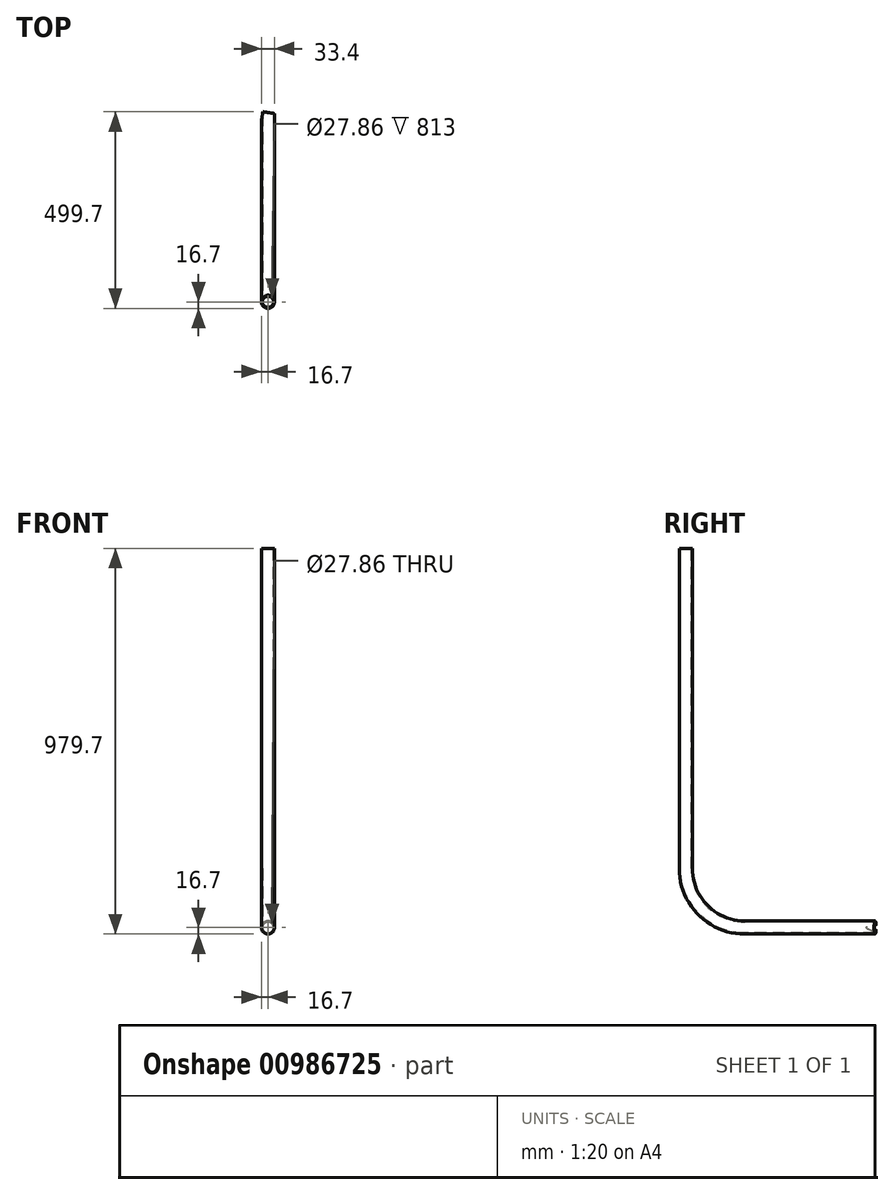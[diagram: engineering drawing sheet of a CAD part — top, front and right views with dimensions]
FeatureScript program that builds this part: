
annotation { "Feature Type Name" : "Feature", "Feature Type Description" : "" }
export const myFeature = defineFeature(function(context is Context, id is Id, definition is map)
    precondition{}
    {
        {
            var Q0;
            Q0=qCreatedBy(makeId("Right.planeOp"),FACE);
            var sketch = newSketch(context, id + "F0", { "sketchPlane" : qUnion([Q0])});
            skLineSegment(sketch, "E0", {"start": v(0, 0) * mm, "end": v(-333.6, 0) * mm});
            skLineSegment(sketch, "E1", {"start": v(-483.6, 150) * mm, "end": v(-483.6, 963) * mm});
            skPoint(sketch, "E2.visualSharp", {"position": v(-483.6, 0) * mm});
            skArc(sketch, "E2.filletArc", {"start": v(-483.6, 150) * mm, "mid": v(-439.67, 43.93) * mm, "end": v(-333.6, 0) * mm});
            skSolve(sketch);
        }
        {
            var Q0;
            Q0=qCreatedBy(makeId("Front.planeOp"),FACE);
            var sketch = newSketch(context, id + "F1", { "sketchPlane" : qUnion([Q0])});
            skCircle(sketch, "E3", {"center": v(0, 0) * mm, "radius": 16.7 * mm});
            skCircle(sketch, "E4.0", {"center": v(0, 0) * mm, "radius": 13.93 * mm});
            skSolve(sketch);
        }
        {
            var Q0;
            Q0=makeQuery(id+"F1.imprint","IMPRINT",FACE,{"disambiguationData":[TD([[makeQuery(id+"F1.imprint","IMPRINT",EDGE,{"derivedFrom":sQuery(id+"F1.wireOp",EDGE,"E3")}),1.0]])]});
            var Q1;
            Q1=sQuery(id+"F0.wireOp",EDGE,"E0");
            var Q2;
            Q2=sQuery(id+"F0.wireOp",EDGE,"E2.filletArc");
            var Q3;
            Q3=sQuery(id+"F0.wireOp",EDGE,"E1");
            sweep(context, id + "F2", {"profiles" : qUnion([Q0]), "path" : qUnion([Q1, Q2, Q3])});
        }
        {
            var Q0;
            Q0=qCreatedBy(makeId("Top.planeOp"),FACE);
            var sketch = newSketch(context, id + "F3", { "sketchPlane" : qUnion([Q0])});
            skLineSegment(sketch, "E5", {"start": v(0, 0) * mm, "end": v(29.63, -4.7) * mm});
            skLineSegment(sketch, "E6", {"start": v(0, 0) * mm, "end": v(16.7, 0) * mm});
            skLineSegment(sketch, "E7", {"start": v(16.7, 0) * mm, "end": v(16.7, -2.65) * mm});
            skLineSegment(sketch, "E8", {"start": v(0, 0) * mm, "end": v(2.57, 16.22) * mm});
            skLineSegment(sketch, "E9.MirrorCS", {"start": v(0, 0) * mm, "end": v(-29.63, 4.7) * mm});
            skLineSegment(sketch, "E10.MirrorCS", {"start": v(-15.88, 5.16) * mm, "end": v(-16.7, 2.65) * mm});
            skLineSegment(sketch, "E11", {"start": v(-16.7, 2.65) * mm, "end": v(-16.7, 0) * mm});
            skLineSegment(sketch, "E12", {"start": v(-16.7, 0) * mm, "end": v(17.86, -5.47) * mm});
            skLineSegment(sketch, "E13", {"start": v(-16.7, 0) * mm, "end": v(16.7, 0) * mm});
            skLineSegment(sketch, "E14", {"start": v(16.7, -5.47) * mm, "end": v(16.7, 0) * mm});
            skLineSegment(sketch, "E15", {"start": v(0, 0) * mm, "end": v(-16.7, 0) * mm});
            skLineSegment(sketch, "E16", {"start": v(-16.7, 0) * mm, "end": v(0, 0) * mm});
            skLineSegment(sketch, "E17", {"start": v(16.7, -5.3) * mm, "end": v(-12.93, -0.6) * mm});
            skLineSegment(sketch, "E18", {"start": v(-12.93, -0.6) * mm, "end": v(-19.43, -41.61) * mm});
            skLineSegment(sketch, "E19", {"start": v(-16.7, 0) * mm, "end": v(-16.7, -32.2) * mm});
            skSolve(sketch);
        }
        {
            var Q0;
            Q0 = qSketchRegion(id + "F3", true);
            extrude(context, id + "F4", {"entities" : qUnion([Q0]), "operationType" : NewBodyOperationType.REMOVE, "endBound" : BoundingType.THROUGH_ALL, "oppositeDirection" : true, "depth" : 25 * mm, "offsetDistance" : 25 * mm, "hasSecondDirection" : true, "secondDirectionBound" : BoundingType.THROUGH_ALL, "secondDirectionOppositeDirection" : false, "secondDirectionDepth" : 25 * mm});
        }
    });
